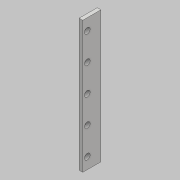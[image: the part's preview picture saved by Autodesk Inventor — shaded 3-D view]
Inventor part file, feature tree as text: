
AUTODESK INVENTOR PART (.ipt)
format: ipt  version: 2018 (Build 220112000, 112)  size: 92,160 bytes
history: native  units: mm
features: sketch x2, other x1, extrude x1, hole x1
ambient origin geometry x8: Origin, YZ Plane, XZ Plane, XY Plane, X Axis, Y Axis, Z Axis, Center Point
bodies: Body1 (feature_tree)
feature tree (5):
  other  "實體1"
  extrude  "擠出1"  Depth=80.0mm
  hole  "孔1"  [1 undecoded]
  sketch  "草圖1"
  sketch  "草圖2"
note: 1 required parameter value undecoded (feature->parameter linkage not recoverable at this tier; creation-order binding heuristic only, values carry confidence <= 0.55)
